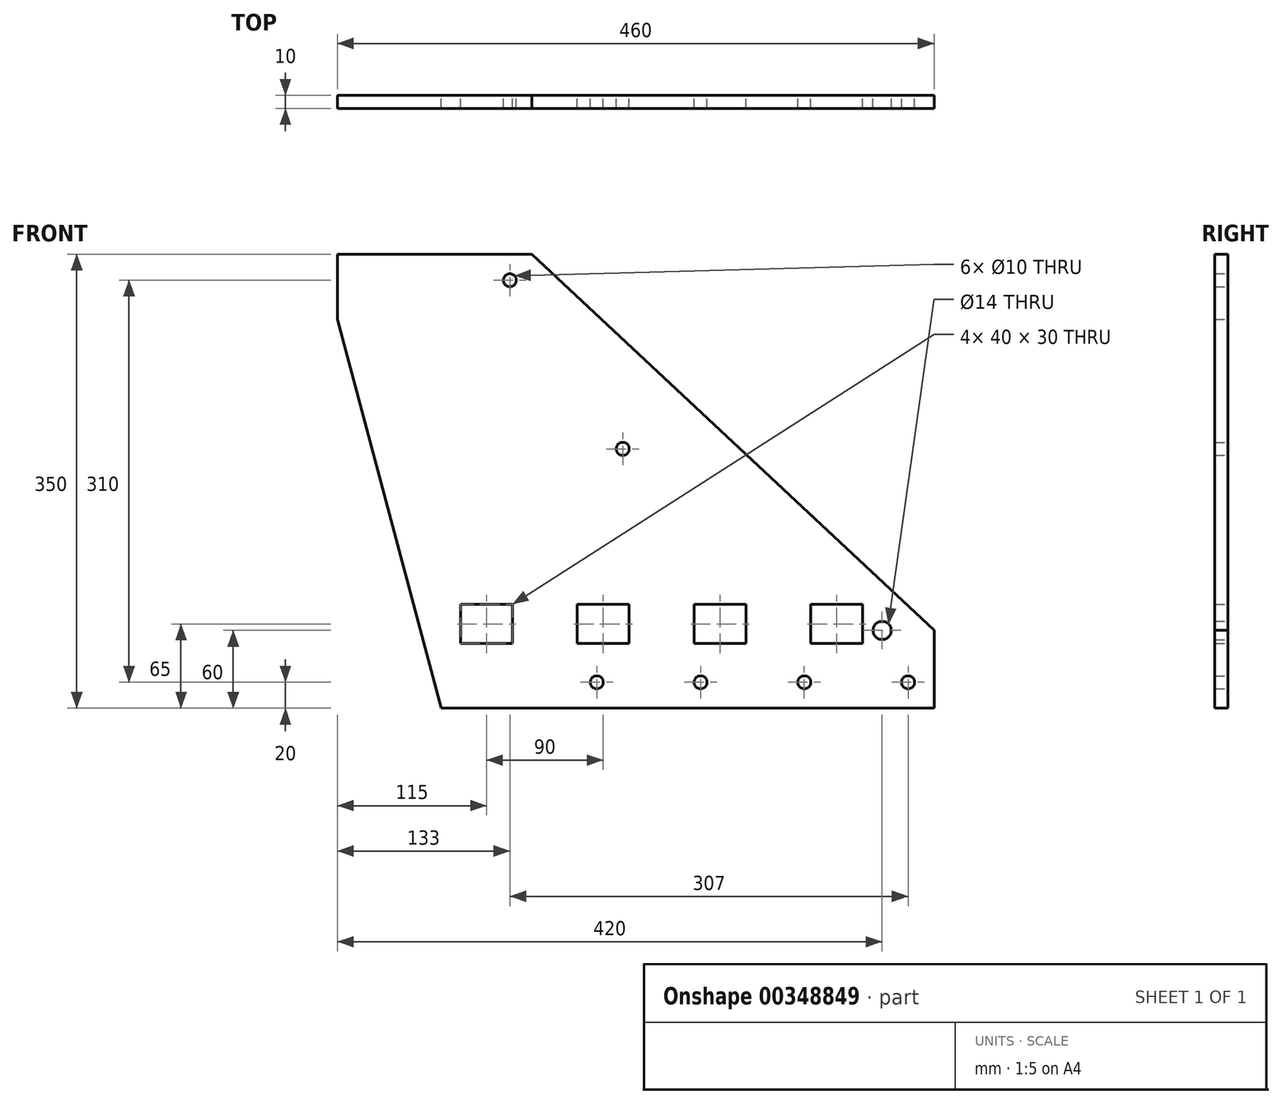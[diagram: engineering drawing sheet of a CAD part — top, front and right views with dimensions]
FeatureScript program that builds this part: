
annotation { "Feature Type Name" : "Feature", "Feature Type Description" : "" }
export const myFeature = defineFeature(function(context is Context, id is Id, definition is map)
    precondition{}
    {
        {
            var Q0;
            Q0=qCreatedBy(makeId("Front.planeOp"),FACE);
            var sketch = newSketch(context, id + "F0", { "sketchPlane" : qUnion([Q0])});
            skLineSegment(sketch, "E0", {"start": v(0, 0) * mm, "end": v(-380, 0) * mm});
            skLineSegment(sketch, "E1", {"start": v(-380, 0) * mm, "end": v(-460, 300) * mm});
            skLineSegment(sketch, "E2", {"start": v(-460, 300) * mm, "end": v(-460, 350) * mm});
            skLineSegment(sketch, "E3", {"start": v(-460, 350) * mm, "end": v(-310, 350) * mm});
            skLineSegment(sketch, "E4", {"start": v(-310, 350) * mm, "end": v(0, 60) * mm});
            skCircle(sketch, "E5", {"center": v(-327, 330) * mm, "radius": 5 * mm});
            skCircle(sketch, "E6", {"center": v(-20, 20) * mm, "radius": 5 * mm});
            skCircle(sketch, "E7.1.0.0", {"center": v(-100, 20) * mm, "radius": 5 * mm});
            skCircle(sketch, "E7.2.0.0", {"center": v(-180, 20) * mm, "radius": 5 * mm});
            skCircle(sketch, "E8.0.3.0", {"center": v(-260, 20) * mm, "radius": 5 * mm});
            skLineSegment(sketch, "E9", {"start": v(-20, 20) * mm, "end": v(-270.96, 20) * mm, "construction": true});
            skCircle(sketch, "E10", {"center": v(-40, 60) * mm, "radius": 7 * mm});
            skLineSegment(sketch, "E11", {"start": v(0, 60) * mm, "end": v(0, 0) * mm});
            skCircle(sketch, "E12", {"center": v(-240, 200) * mm, "radius": 5 * mm});
            skLineSegment(sketch, "E13", {"start": v(-55, 50) * mm, "end": v(-95, 50) * mm});
            skLineSegment(sketch, "E14", {"start": v(-95, 50) * mm, "end": v(-95, 80) * mm});
            skLineSegment(sketch, "E15", {"start": v(-95, 80) * mm, "end": v(-55, 80) * mm});
            skLineSegment(sketch, "E16", {"start": v(-55, 80) * mm, "end": v(-55, 50) * mm});
            skLineSegment(sketch, "E17.1.0.0", {"start": v(-185, 80) * mm, "end": v(-145, 80) * mm});
            skLineSegment(sketch, "E17.1.0.1", {"start": v(-145, 80) * mm, "end": v(-145, 50) * mm});
            skLineSegment(sketch, "E17.1.0.2", {"start": v(-145, 50) * mm, "end": v(-185, 50) * mm});
            skLineSegment(sketch, "E17.1.0.3", {"start": v(-185, 50) * mm, "end": v(-185, 80) * mm});
            skLineSegment(sketch, "E17.2.0.0", {"start": v(-275, 80) * mm, "end": v(-235, 80) * mm});
            skLineSegment(sketch, "E17.2.0.1", {"start": v(-235, 80) * mm, "end": v(-235, 50) * mm});
            skLineSegment(sketch, "E17.2.0.2", {"start": v(-235, 50) * mm, "end": v(-275, 50) * mm});
            skLineSegment(sketch, "E17.2.0.3", {"start": v(-275, 50) * mm, "end": v(-275, 80) * mm});
            skLineSegment(sketch, "E17.3.0.0", {"start": v(-365, 80) * mm, "end": v(-325, 80) * mm});
            skLineSegment(sketch, "E17.3.0.1", {"start": v(-325, 80) * mm, "end": v(-325, 50) * mm});
            skLineSegment(sketch, "E17.3.0.2", {"start": v(-325, 50) * mm, "end": v(-365, 50) * mm});
            skLineSegment(sketch, "E17.3.0.3", {"start": v(-365, 50) * mm, "end": v(-365, 80) * mm});
            skLineSegment(sketch, "E17.direction1", {"start": v(-95, 50) * mm, "end": v(-185, 50) * mm, "construction": true});
            skSolve(sketch);
        }
        {
            var Q0;
            Q0=makeQuery(id+"F0.imprint","IMPRINT",FACE,{"disambiguationData":[TD([[makeQuery(id+"F0.imprint","IMPRINT",EDGE,{"derivedFrom":sQuery(id+"F0.wireOp",EDGE,"E0")}),-1.0]])]});
            extrude(context, id + "F1", {"entities" : qUnion([Q0]), "depth" : 10 * mm});
        }
    });
